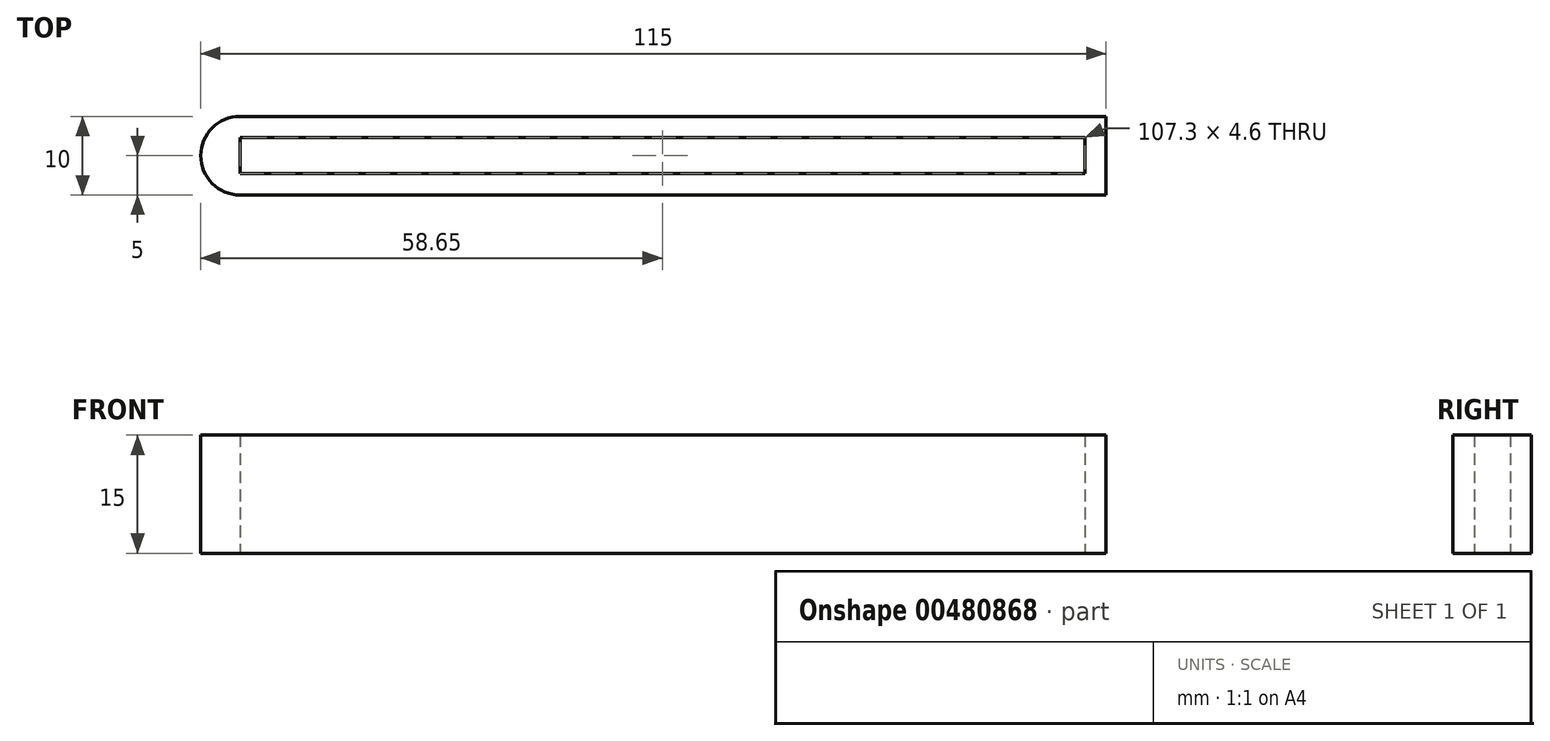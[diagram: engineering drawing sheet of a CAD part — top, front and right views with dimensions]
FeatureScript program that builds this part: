
annotation { "Feature Type Name" : "Feature", "Feature Type Description" : "" }
export const myFeature = defineFeature(function(context is Context, id is Id, definition is map)
    precondition{}
    {
        {
            var Q0;
            Q0=qCreatedBy(makeId("Top.planeOp"),FACE);
            var sketch = newSketch(context, id + "F0", { "sketchPlane" : qUnion([Q0])});
            skLineSegment(sketch, "E0.bottom", {"start": v(-55, -5) * mm, "end": v(55, -5) * mm});
            skLineSegment(sketch, "E0.top", {"start": v(-55, 5) * mm, "end": v(55, 5) * mm});
            skLineSegment(sketch, "E0.left", {"start": v(-55, -5) * mm, "end": v(-55, 5) * mm});
            skLineSegment(sketch, "E0.right", {"start": v(55, -5) * mm, "end": v(55, 5) * mm});
            skPoint(sketch, "E0.middle", {"position": v(0, 0) * mm});
            skArc(sketch, "E1", {"start": v(-55, 5) * mm, "mid": v(-60, 0) * mm, "end": v(-55, -5) * mm});
            skLineSegment(sketch, "E2.0", {"start": v(-55, 2.3) * mm, "end": v(52.3, 2.3) * mm});
            skArc(sketch, "E2.1", {"start": v(-55, 2.3) * mm, "mid": v(-57.3, 0) * mm, "end": v(-55, -2.3) * mm});
            skLineSegment(sketch, "E2.2", {"start": v(-55, -2.3) * mm, "end": v(52.3, -2.3) * mm});
            skLineSegment(sketch, "E2.3", {"start": v(52.3, -2.3) * mm, "end": v(52.3, 2.3) * mm});
            skSolve(sketch);
        }
        {
            var Q0;
            Q0 = qSketchRegion(id + "F0", true);
            var Q1;
            {var subQ0=sQuery(id+"F0.wireOp",EDGE,"E2.1");Q1=makeQuery(id+"F0.imprint","IMPRINT",FACE,{"disambiguationData":[TD([[makeQuery(id+"F0.imprint","IMPRINT",EDGE,{"derivedFrom":subQ0}),1.0]])]});}
            extrude(context, id + "F1", {"entities" : qUnion([Q0, Q1]), "depth" : 15 * mm});
        }
    });
